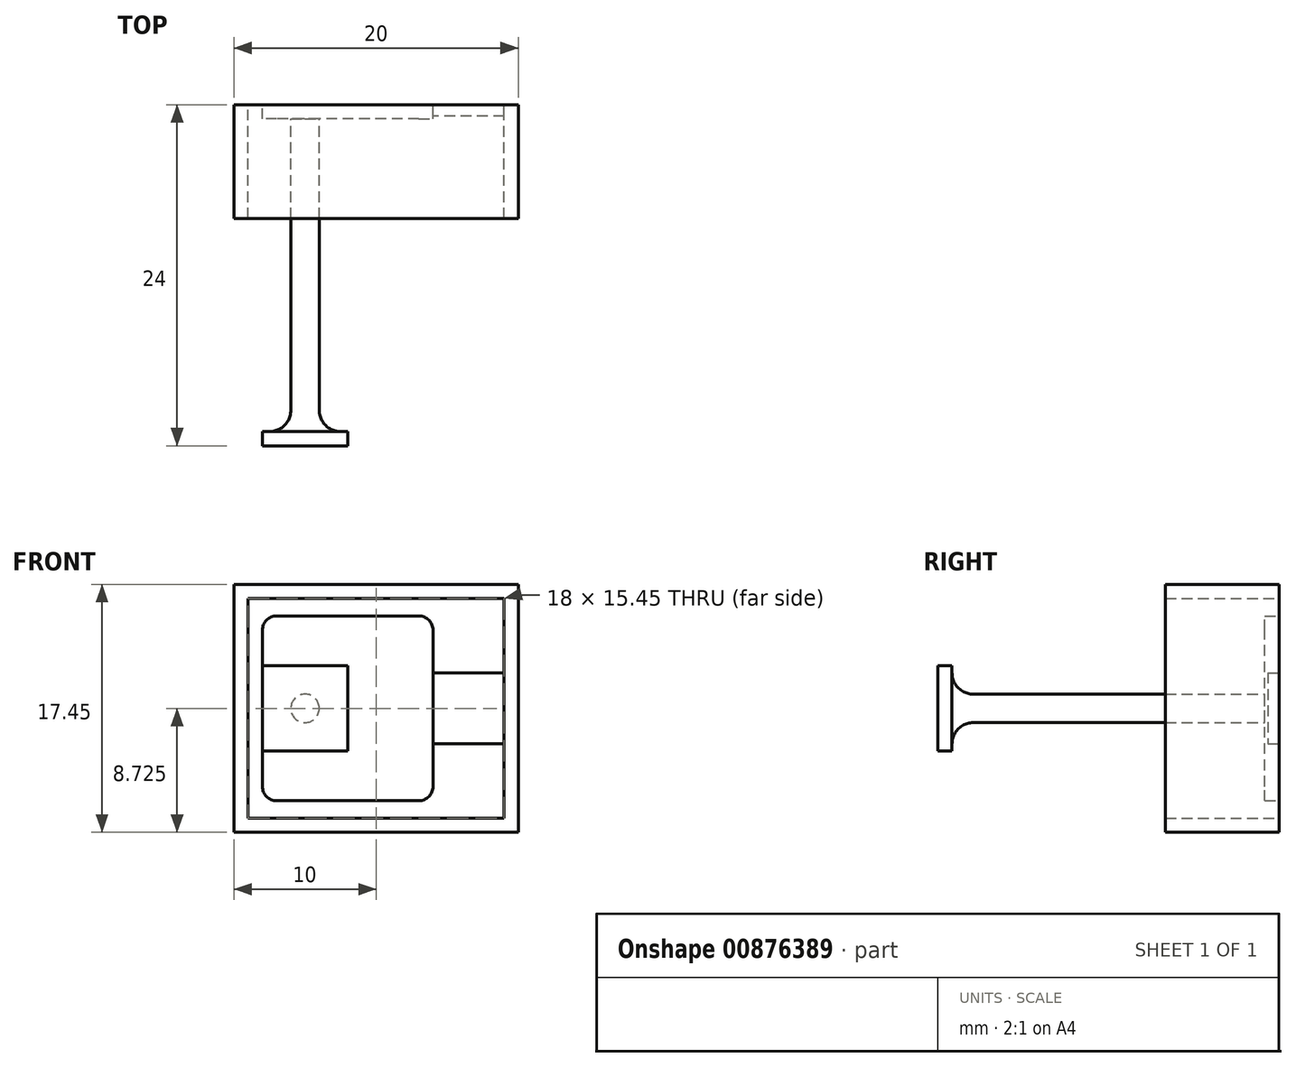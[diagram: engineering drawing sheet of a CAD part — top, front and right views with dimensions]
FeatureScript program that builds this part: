
annotation { "Feature Type Name" : "Feature", "Feature Type Description" : "" }
export const myFeature = defineFeature(function(context is Context, id is Id, definition is map)
    precondition{}
    {
        {
            var Q0;
            Q0=qCreatedBy(makeId("Front.planeOp"),FACE);
            var sketch = newSketch(context, id + "F0", { "sketchPlane" : qUnion([Q0])});
            skLineSegment(sketch, "E0", {"start": v(0, 17.45) * mm, "end": v(0, 0) * mm});
            skLineSegment(sketch, "E1", {"start": v(0, 0) * mm, "end": v(20, 0) * mm});
            skLineSegment(sketch, "E2", {"start": v(20, 0) * mm, "end": v(20, 17.45) * mm});
            skLineSegment(sketch, "E3", {"start": v(20, 17.45) * mm, "end": v(0, 17.45) * mm});
            skLineSegment(sketch, "E4", {"start": v(14, 11.23) * mm, "end": v(14, 15.23) * mm});
            skLineSegment(sketch, "E5", {"start": v(14, 15.23) * mm, "end": v(2, 15.23) * mm});
            skLineSegment(sketch, "E6", {"start": v(2, 2.22) * mm, "end": v(14, 2.22) * mm});
            skLineSegment(sketch, "E7", {"start": v(14, 2.22) * mm, "end": v(14, 6.22) * mm});
            skLineSegment(sketch, "E8", {"start": v(19, 6.22) * mm, "end": v(19, 1) * mm});
            skLineSegment(sketch, "E9", {"start": v(1, 1) * mm, "end": v(1, 16.45) * mm});
            skLineSegment(sketch, "E10", {"start": v(19, 16.45) * mm, "end": v(19, 11.23) * mm});
            skLineSegment(sketch, "E11", {"start": v(19, 16.45) * mm, "end": v(1, 16.45) * mm});
            skLineSegment(sketch, "E12", {"start": v(1, 1) * mm, "end": v(19, 1) * mm});
            skLineSegment(sketch, "E13", {"start": v(19, 6.22) * mm, "end": v(14, 6.22) * mm});
            skLineSegment(sketch, "E14", {"start": v(19, 11.23) * mm, "end": v(14, 11.23) * mm});
            skLineSegment(sketch, "E15", {"start": v(2, 15.23) * mm, "end": v(2, 2.22) * mm});
            skLineSegment(sketch, "E16", {"start": v(19, 11.23) * mm, "end": v(19, 6.22) * mm});
            skLineSegment(sketch, "E17", {"start": v(2, 11.72) * mm, "end": v(8, 11.72) * mm});
            skLineSegment(sketch, "E18", {"start": v(8, 11.72) * mm, "end": v(8, 5.72) * mm});
            skLineSegment(sketch, "E19", {"start": v(8, 5.72) * mm, "end": v(2, 5.72) * mm});
            skCircle(sketch, "E20", {"center": v(5, 8.72) * mm, "radius": 1 * mm});
            skPoint(sketch, "E20.centerSnap0", {"position": v(1, 8.72) * mm});
            skLineSegment(sketch, "E21", {"start": v(2, 11.72) * mm, "end": v(8, 5.72) * mm, "construction": true});
            skLineSegment(sketch, "E22", {"start": v(5, 8.72) * mm, "end": v(19, 8.72) * mm, "construction": true});
            skSolve(sketch);
        }
        {
            var Q0;
            Q0 = qSketchRegion(id + "F0", true);
            extrude(context, id + "F1", {"entities" : qUnion([Q0]), "depth" : 8 * mm, "offsetDistance" : 25.4 * mm});
        }
        {
            var Q0;
            Q0=makeQuery(id+"F0.imprint","IMPRINT",FACE,{"disambiguationData":[TD([[makeQuery(id+"F0.imprint","IMPRINT",EDGE,{"derivedFrom":sQuery(id+"F0.wireOp",EDGE,"E4")}),1.0]])]});
            var Q1;
            {var subQ0=sQuery(id+"F0.wireOp",EDGE,"E17");Q1=makeQuery(id+"F0.imprint","IMPRINT",FACE,{"disambiguationData":[TD([[makeQuery(id+"F0.imprint","IMPRINT",EDGE,{"derivedFrom":subQ0}),-1.0]])]});}
            extrude(context, id + "F2", {"entities" : qUnion([Q0, Q1]), "operationType" : NewBodyOperationType.ADD, "depth" : 1 * mm, "offsetDistance" : 25 * mm});
        }
        {
            var Q0;
            Q0=makeQuery(id+"F0.imprint","IMPRINT",FACE,{"disambiguationData":[TD([[makeQuery(id+"F0.imprint","IMPRINT",EDGE,{"derivedFrom":sQuery(id+"F0.wireOp",EDGE,"E20")}),1.0]])]});
            extrude(context, id + "F3", {"entities" : qUnion([Q0]), "operationType" : NewBodyOperationType.ADD, "depth" : 24 * mm, "offsetDistance" : 25 * mm});
        }
        {
            var Q0;
            Q0=makeQuery(id+"F3.opExtrude","CAP_FACE",FACE,{"disambiguationData":[OSD([sQuery(id+"F0.wireOp",EDGE,"E20")])],"isStart":false});
            var sketch = newSketch(context, id + "F4", { "sketchPlane" : qUnion([Q0])});
            skLineSegment(sketch, "E23.bottom", {"start": v(2, 11.72) * mm, "end": v(8, 11.73) * mm});
            skLineSegment(sketch, "E23.top", {"start": v(2, 5.73) * mm, "end": v(8, 5.73) * mm});
            skLineSegment(sketch, "E23.left", {"start": v(2, 11.72) * mm, "end": v(2, 5.73) * mm});
            skLineSegment(sketch, "E23.right", {"start": v(8, 11.73) * mm, "end": v(8, 5.73) * mm});
            skPoint(sketch, "E23.middle", {"position": v(5, 8.72) * mm});
            skSolve(sketch);
        }
        {
            var Q0;
            Q0 = qSketchRegion(id + "F4", true);
            extrude(context, id + "F5", {"entities" : qUnion([Q0]), "operationType" : NewBodyOperationType.ADD, "oppositeDirection" : true, "depth" : 1 * mm, "offsetDistance" : 25 * mm});
        }
        {
            var Q0;
            Q0=makeQuery(id+"F5.boolean.opBoolean","INTERSECT",EDGE,{"derivedFrom":[makeQuery(id+"F3.opExtrude","SWEPT_FACE",FACE,{"disambiguationData":[OSD([sQuery(id+"F0.wireOp",EDGE,"E20")])]}),makeQuery(id+"F5.opExtrude","CAP_FACE",FACE,{"disambiguationData":[OSD([sQuery(id+"F4.wireOp",EDGE,"E23.bottom"),sQuery(id+"F4.wireOp",EDGE,"E23.top"),sQuery(id+"F4.wireOp",EDGE,"E23.left"),sQuery(id+"F4.wireOp",EDGE,"E23.right")])],"isStart":false})]});
            var Q1;
            Q1=makeQuery(id+"F2.opExtrude","CAP_EDGE",EDGE,{"disambiguationData":[OSD([sQuery(id+"F0.wireOp",EDGE,"E20")])],"isStart":false});
            fillet(context, id + "F6", {"entities" : qUnion([Q0, Q1]), "radius" : 1.5 * mm, "tangentPropagation" : true, "allowEdgeOverflow" : false});
        }
        {
            var Q0;
            Q0=makeQuery(id+"F2.opExtrude","CAP_FACE",FACE,{"disambiguationData":[OSD([sQuery(id+"F0.wireOp",EDGE,"E4"),sQuery(id+"F0.wireOp",EDGE,"E5"),sQuery(id+"F0.wireOp",EDGE,"E6"),sQuery(id+"F0.wireOp",EDGE,"E7"),sQuery(id+"F0.wireOp",EDGE,"E13"),sQuery(id+"F0.wireOp",EDGE,"E14"),sQuery(id+"F0.wireOp",EDGE,"E15"),sQuery(id+"F0.wireOp",EDGE,"E16"),sQuery(id+"F0.wireOp",EDGE,"E20")])],"isStart":false});
            var sketch = newSketch(context, id + "F7", { "sketchPlane" : qUnion([Q0])});
            skLineSegment(sketch, "E24.bottom", {"start": v(14, 11.23) * mm, "end": v(19, 11.23) * mm});
            skLineSegment(sketch, "E24.top", {"start": v(14, 6.22) * mm, "end": v(19, 6.22) * mm});
            skLineSegment(sketch, "E24.left", {"start": v(14, 11.23) * mm, "end": v(14, 6.22) * mm});
            skLineSegment(sketch, "E24.right", {"start": v(19, 11.23) * mm, "end": v(19, 6.22) * mm});
            skSolve(sketch);
        }
        {
            var Q0;
            Q0 = qSketchRegion(id + "F7", true);
            extrude(context, id + "F8", {"entities" : qUnion([Q0]), "operationType" : NewBodyOperationType.REMOVE, "oppositeDirection" : true, "depth" : 0.2 * mm, "offsetDistance" : 25 * mm});
        }
        {
            var Q0;
            Q0=makeQuery(id+"F2.opExtrude","SWEPT_EDGE",EDGE,{"disambiguationData":[OSD([sQuery(id+"F0.wireOp",EDGE,"E5"),sQuery(id+"F0.wireOp",EDGE,"E15")])]});
            var Q1;
            Q1=makeQuery(id+"F2.opExtrude","SWEPT_EDGE",EDGE,{"disambiguationData":[OSD([sQuery(id+"F0.wireOp",EDGE,"E4"),sQuery(id+"F0.wireOp",EDGE,"E5")])]});
            var Q2;
            Q2=makeQuery(id+"F2.opExtrude","SWEPT_EDGE",EDGE,{"disambiguationData":[OSD([sQuery(id+"F0.wireOp",EDGE,"E6"),sQuery(id+"F0.wireOp",EDGE,"E15")])]});
            var Q3;
            Q3=makeQuery(id+"F2.opExtrude","SWEPT_EDGE",EDGE,{"disambiguationData":[OSD([sQuery(id+"F0.wireOp",EDGE,"E6"),sQuery(id+"F0.wireOp",EDGE,"E7")])]});
            fillet(context, id + "F9", {"entities" : qUnion([Q0, Q1, Q2, Q3]), "radius" : 1 * mm, "tangentPropagation" : true, "allowEdgeOverflow" : false});
        }
    });
